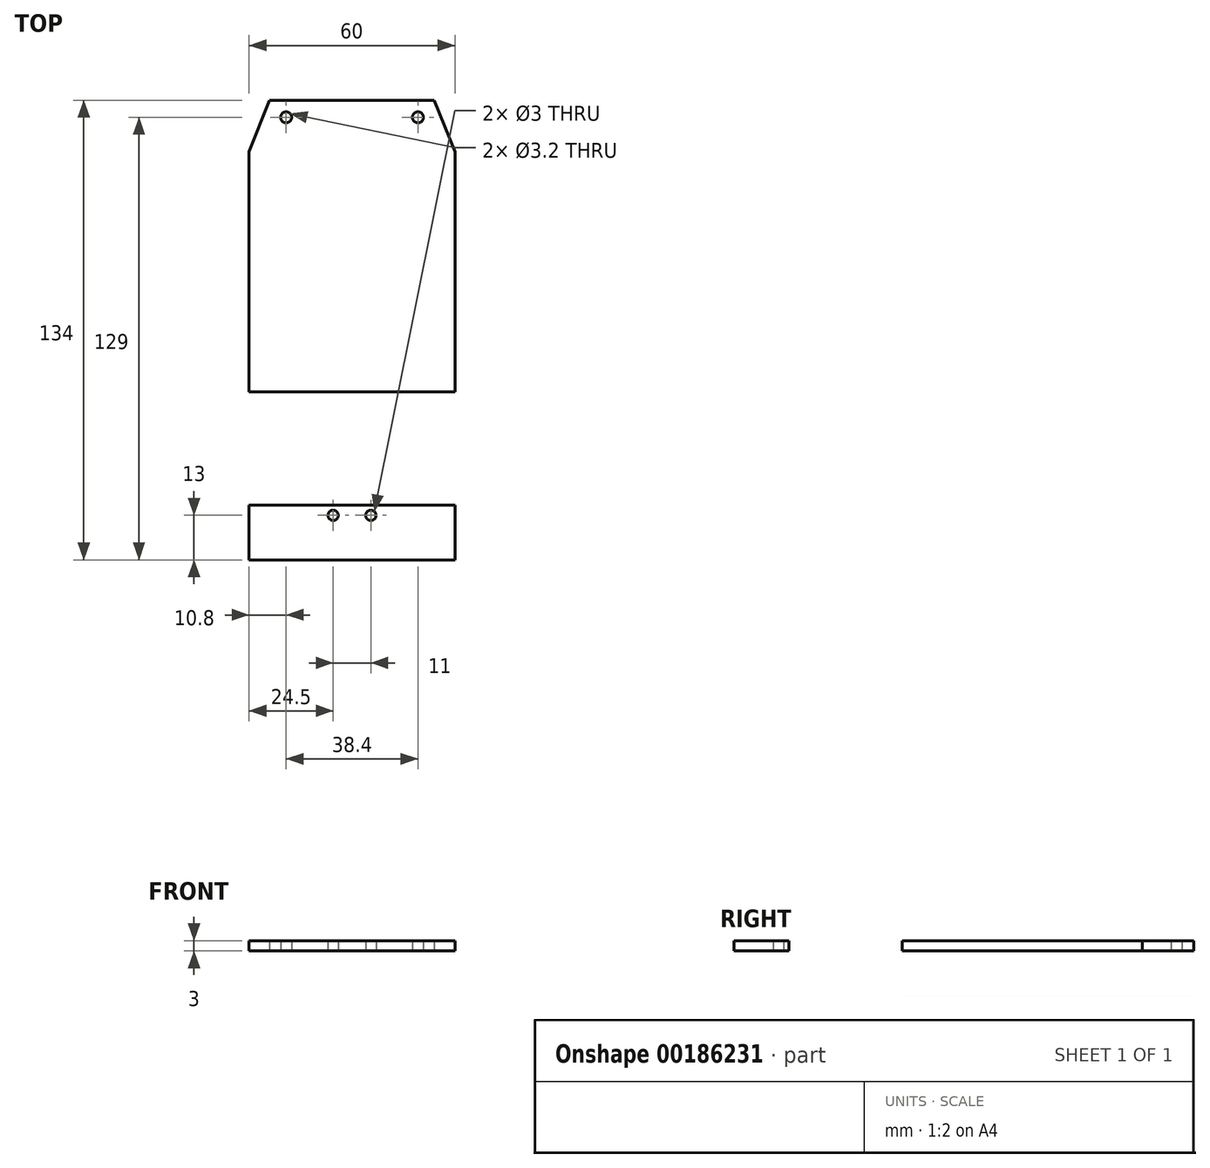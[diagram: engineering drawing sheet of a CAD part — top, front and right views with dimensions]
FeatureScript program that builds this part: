
annotation { "Feature Type Name" : "Feature", "Feature Type Description" : "" }
export const myFeature = defineFeature(function(context is Context, id is Id, definition is map)
    precondition{}
    {
        {
            var Q0;
            Q0=qCreatedBy(makeId("Top.planeOp"),FACE);
            var sketch = newSketch(context, id + "F0", { "sketchPlane" : qUnion([Q0])});
            skLineSegment(sketch, "E0.bottom", {"start": v(-30, 42.5) * mm, "end": v(30, 42.5) * mm});
            skLineSegment(sketch, "E0.top", {"start": v(-30, -42.5) * mm, "end": v(30, -42.5) * mm});
            skLineSegment(sketch, "E0.left", {"start": v(-30, 42.5) * mm, "end": v(-30, -42.5) * mm});
            skLineSegment(sketch, "E0.right", {"start": v(30, 42.5) * mm, "end": v(30, -42.5) * mm});
            skCircle(sketch, "E1", {"center": v(-19.2, 37.5) * mm, "radius": 1.6 * mm});
            skCircle(sketch, "E2", {"center": v(19.2, 37.5) * mm, "radius": 1.6 * mm});
            skLineSegment(sketch, "E3", {"start": v(-30, 27.5) * mm, "end": v(-24, 42.5) * mm});
            skLineSegment(sketch, "E4", {"start": v(24, 42.5) * mm, "end": v(30, 27.5) * mm});
            skSolve(sketch);
        }
        {
            var Q0;
            {var subQ1=sQuery(id+"F0.wireOp",EDGE,"E0.top");Q0=makeQuery(id+"F0.imprint","IMPRINT",FACE,{"disambiguationData":[TD([[makeQuery(id+"F0.imprint","IMPRINT",EDGE,{"derivedFrom":subQ1}),1.0]])]});}
            extrude(context, id + "F1", {"entities" : qUnion([Q0]), "depth" : 3 * mm});
        }
        {
            var Q0;
            Q0=qCreatedBy(makeId("Top.planeOp"),FACE);
            var sketch = newSketch(context, id + "F2", { "sketchPlane" : qUnion([Q0])});
            skLineSegment(sketch, "E5.bottom", {"start": v(-30, -75.5) * mm, "end": v(30, -75.5) * mm});
            skLineSegment(sketch, "E5.top", {"start": v(-30, -91.5) * mm, "end": v(30, -91.5) * mm});
            skLineSegment(sketch, "E5.left", {"start": v(-30, -75.5) * mm, "end": v(-30, -91.5) * mm});
            skLineSegment(sketch, "E5.right", {"start": v(30, -75.5) * mm, "end": v(30, -91.5) * mm});
            skCircle(sketch, "E6", {"center": v(-5.5, -78.5) * mm, "radius": 1.5 * mm});
            skCircle(sketch, "E7", {"center": v(5.5, -78.5) * mm, "radius": 1.5 * mm});
            skSolve(sketch);
        }
        {
            var Q0;
            Q0=makeQuery(id+"F2.imprint","IMPRINT",FACE,{"disambiguationData":[TD([[makeQuery(id+"F2.imprint","IMPRINT",EDGE,{"derivedFrom":sQuery(id+"F2.wireOp",EDGE,"E5.bottom")}),-1.0]])]});
            extrude(context, id + "F3", {"entities" : qUnion([Q0]), "depth" : 3 * mm});
        }
    });
